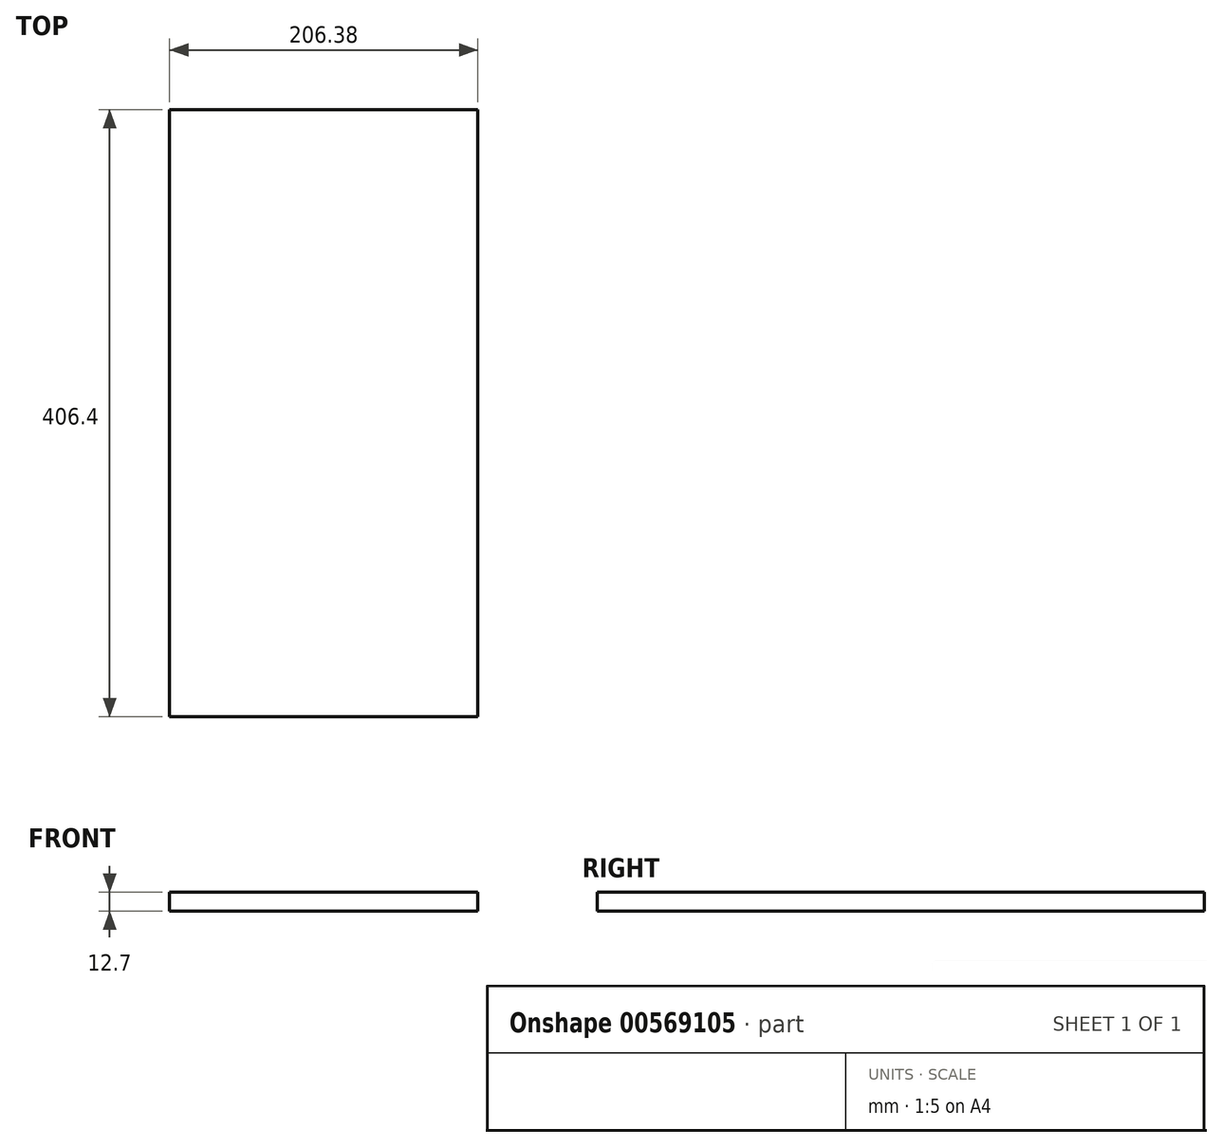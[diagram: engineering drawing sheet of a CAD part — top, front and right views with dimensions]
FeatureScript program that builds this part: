
annotation { "Feature Type Name" : "Feature", "Feature Type Description" : "" }
export const myFeature = defineFeature(function(context is Context, id is Id, definition is map)
    precondition{}
    {
        {
            var Q0;
            Q0=qCreatedBy(makeId("Top.planeOp"),FACE);
            var sketch = newSketch(context, id + "F0", { "sketchPlane" : qUnion([Q0])});
            skLineSegment(sketch, "E0.bottom", {"start": v(103.19, 203.2) * mm, "end": v(-103.19, 203.2) * mm});
            skLineSegment(sketch, "E0.top", {"start": v(103.19, -203.2) * mm, "end": v(-103.19, -203.2) * mm});
            skLineSegment(sketch, "E0.left", {"start": v(103.19, 203.2) * mm, "end": v(103.19, -203.2) * mm});
            skLineSegment(sketch, "E0.right", {"start": v(-103.19, 203.2) * mm, "end": v(-103.19, -203.2) * mm});
            skPoint(sketch, "E0.middle", {"position": v(0, 0) * mm});
            skSolve(sketch);
        }
        {
            var Q0;
            Q0=makeQuery(id+"F0.imprint","IMPRINT",FACE,{"disambiguationData":[TD([[makeQuery(id+"F0.imprint","IMPRINT",EDGE,{"derivedFrom":sQuery(id+"F0.wireOp",EDGE,"E0.bottom")}),1.0]])]});
            extrude(context, id + "F1", {"entities" : qUnion([Q0]), "endBound" : BoundingType.SYMMETRIC, "depth" : 12.7 * mm, "offsetDistance" : 25.4 * mm});
        }
    });
